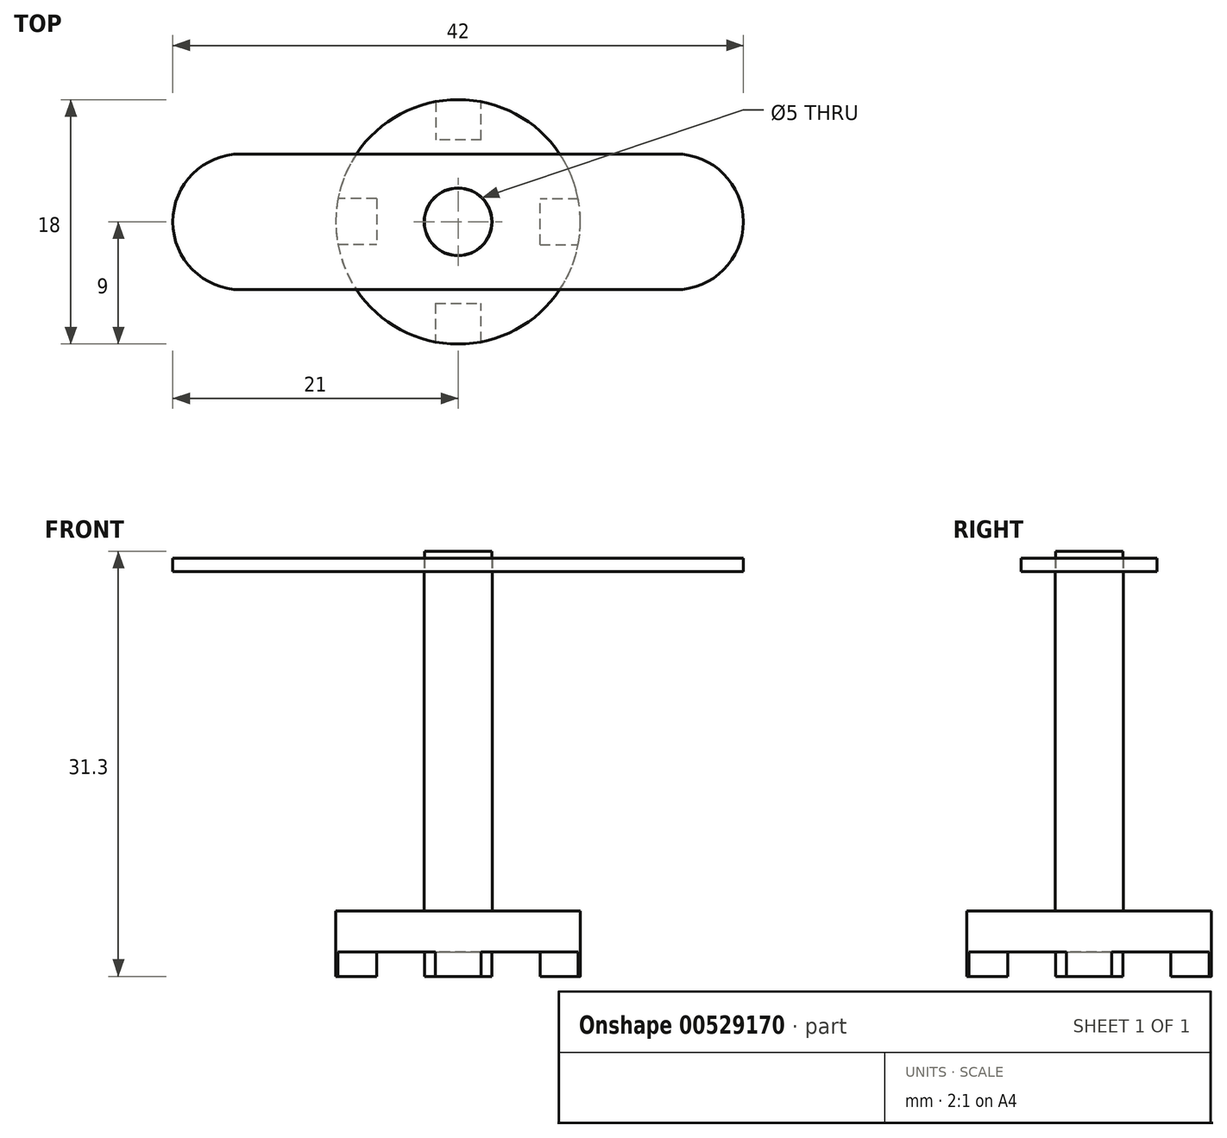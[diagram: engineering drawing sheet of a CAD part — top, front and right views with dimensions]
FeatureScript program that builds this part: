
annotation { "Feature Type Name" : "Feature", "Feature Type Description" : "" }
export const myFeature = defineFeature(function(context is Context, id is Id, definition is map)
    precondition{}
    {
        {
            var Q0;
            Q0=qCreatedBy(makeId("Top.planeOp"),FACE);
            var sketch = newSketch(context, id + "F0", { "sketchPlane" : qUnion([Q0])});
            skCircle(sketch, "E0", {"center": v(0, 0) * mm, "radius": 5 * mm});
            skCircle(sketch, "E1", {"center": v(0, 0) * mm, "radius": 9 * mm});
            skCircle(sketch, "E2", {"center": v(0, 0) * mm, "radius": 2.5 * mm});
            skSolve(sketch);
        }
        {
            var Q0;
            Q0=makeQuery(id+"F0.imprint","IMPRINT",FACE,{"disambiguationData":[TD([[makeQuery(id+"F0.imprint","IMPRINT",EDGE,{"derivedFrom":sQuery(id+"F0.wireOp",EDGE,"E2")}),1.0]])]});
            extrude(context, id + "F1", {"entities" : qUnion([Q0]), "depth" : 25 * mm, "offsetDistance" : 25 * mm});
        }
        {
            var Q0;
            Q0=makeQuery(id+"F0.imprint","IMPRINT",FACE,{"disambiguationData":[TD([[makeQuery(id+"F0.imprint","IMPRINT",EDGE,{"derivedFrom":sQuery(id+"F0.wireOp",EDGE,"E0")}),-1.0]])]});
            var Q1;
            Q1=makeQuery(id+"F0.imprint","IMPRINT",FACE,{"disambiguationData":[TD([[makeQuery(id+"F0.imprint","IMPRINT",EDGE,{"derivedFrom":sQuery(id+"F0.wireOp",EDGE,"E0")}),1.0]])]});
            var Q2;
            Q2=makeQuery(id+"F0.imprint","IMPRINT",FACE,{"disambiguationData":[TD([[makeQuery(id+"F0.imprint","IMPRINT",EDGE,{"derivedFrom":sQuery(id+"F0.wireOp",EDGE,"E2")}),1.0]])]});
            extrude(context, id + "F2", {"entities" : qUnion([Q0, Q1, Q2]), "operationType" : NewBodyOperationType.ADD, "oppositeDirection" : true, "depth" : 3 * mm, "offsetDistance" : 25 * mm});
        }
        {
            var Q0;
            Q0=makeQuery(id+"F2.opExtrude","CAP_FACE",FACE,{"disambiguationData":[OSD([sQuery(id+"F0.wireOp",EDGE,"E1")])],"isStart":false});
            var sketch = newSketch(context, id + "F3", { "sketchPlane" : qUnion([Q0])});
            skCircle(sketch, "E3", {"center": v(0, 0) * mm, "radius": 2.48 * mm});
            skLineSegment(sketch, "E4", {"start": v(0, 0) * mm, "end": v(0, 6) * mm, "construction": true});
            skLineSegment(sketch, "E5", {"start": v(-1.68, 6) * mm, "end": v(-1.68, 13) * mm});
            skLineSegment(sketch, "E6", {"start": v(-1.68, 13) * mm, "end": v(1.67, 13) * mm});
            skLineSegment(sketch, "E7", {"start": v(1.67, 13) * mm, "end": v(1.67, 6) * mm});
            skLineSegment(sketch, "E8", {"start": v(-1.68, 6) * mm, "end": v(1.67, 6) * mm});
            skLineSegment(sketch, "E9.1.0", {"start": v(-6, -1.7) * mm, "end": v(-13, -1.7) * mm});
            skLineSegment(sketch, "E9.1.1", {"start": v(-13, 1.65) * mm, "end": v(-6, 1.65) * mm});
            skLineSegment(sketch, "E9.1.2", {"start": v(-13, -1.7) * mm, "end": v(-13, 1.65) * mm});
            skLineSegment(sketch, "E9.1.3", {"start": v(-6, -1.7) * mm, "end": v(-6, 1.65) * mm});
            skLineSegment(sketch, "E9.2.0", {"start": v(1.7, -6.02) * mm, "end": v(1.7, -13.02) * mm});
            skLineSegment(sketch, "E9.2.1", {"start": v(-1.65, -13.02) * mm, "end": v(-1.65, -6.03) * mm});
            skLineSegment(sketch, "E9.2.2", {"start": v(1.7, -13.02) * mm, "end": v(-1.65, -13.02) * mm});
            skLineSegment(sketch, "E9.2.3", {"start": v(1.7, -6.02) * mm, "end": v(-1.65, -6.03) * mm});
            skPoint(sketch, "E9.center", {"position": v(0.01, -0.01) * mm});
            skLineSegment(sketch, "E10.1.3.0", {"start": v(6.02, 1.67) * mm, "end": v(13.02, 1.67) * mm});
            skLineSegment(sketch, "E10.3.3.0", {"start": v(13.02, -1.67) * mm, "end": v(6.03, -1.67) * mm});
            skLineSegment(sketch, "E10.6.3.0", {"start": v(13.02, 1.67) * mm, "end": v(13.02, -1.67) * mm});
            skLineSegment(sketch, "E10.9.3.0", {"start": v(6.02, 1.67) * mm, "end": v(6.03, -1.67) * mm});
            skSolve(sketch);
        }
        {
            var Q0;
            Q0=makeQuery(id+"F3.imprint","IMPRINT",FACE,{"disambiguationData":[TD([[makeQuery(id+"F3.imprint","IMPRINT",EDGE,{"derivedFrom":sQuery(id+"F3.wireOp",EDGE,"E3")}),1.0]])]});
            var Q1;
            {var subQ0=sQuery(id+"F3.wireOp",EDGE,"E9.1.3");Q1=makeQuery(id+"F3.imprint","IMPRINT",FACE,{"disambiguationData":[TD([[makeQuery(id+"F3.imprint","IMPRINT",EDGE,{"derivedFrom":subQ0}),1.0]])]});}
            var Q2;
            {var subQ0=sQuery(id+"F3.wireOp",EDGE,"E8");Q2=makeQuery(id+"F3.imprint","IMPRINT",FACE,{"disambiguationData":[TD([[makeQuery(id+"F3.imprint","IMPRINT",EDGE,{"derivedFrom":subQ0}),1.0]])]});}
            var Q3;
            {var subQ0=sQuery(id+"F3.wireOp",EDGE,"E10.9.3.0");Q3=makeQuery(id+"F3.imprint","IMPRINT",FACE,{"disambiguationData":[TD([[makeQuery(id+"F3.imprint","IMPRINT",EDGE,{"derivedFrom":subQ0}),1.0]])]});}
            var Q4;
            {var subQ0=sQuery(id+"F3.wireOp",EDGE,"E9.2.3");Q4=makeQuery(id+"F3.imprint","IMPRINT",FACE,{"disambiguationData":[TD([[makeQuery(id+"F3.imprint","IMPRINT",EDGE,{"derivedFrom":subQ0}),1.0]])]});}
            extrude(context, id + "F4", {"entities" : qUnion([Q0, Q1, Q2, Q3, Q4]), "operationType" : NewBodyOperationType.ADD, "depth" : 1.8 * mm, "offsetDistance" : 25 * mm});
        }
        {
            var Q0;
            Q0=makeQuery(id+"F1.opExtrude","CAP_FACE",FACE,{"disambiguationData":[OSD([sQuery(id+"F0.wireOp",EDGE,"E2")])],"isStart":false});
            var sketch = newSketch(context, id + "F5", { "sketchPlane" : qUnion([Q0])});
            skCircle(sketch, "E11", {"center": v(0, 0) * mm, "radius": 2.48 * mm});
            skLineSegment(sketch, "E12", {"start": v(0, 0) * mm, "end": v(-16, 0) * mm, "construction": true});
            skLineSegment(sketch, "E13", {"start": v(0, 0) * mm, "end": v(16, 0) * mm, "construction": true});
            skArc(sketch, "E14", {"start": v(-16, 5) * mm, "mid": v(-21, 0) * mm, "end": v(-16, -5) * mm});
            skArc(sketch, "E15", {"start": v(16, -5) * mm, "mid": v(21, 0) * mm, "end": v(16, 5) * mm});
            skLineSegment(sketch, "E16", {"start": v(-16, 5) * mm, "end": v(16, 5) * mm});
            skLineSegment(sketch, "E17", {"start": v(16, -5) * mm, "end": v(-16, -5) * mm});
            skCircle(sketch, "E18", {"center": v(0, 0) * mm, "radius": 4 * mm});
            skSolve(sketch);
        }
        {
            var Q0;
            Q0=makeQuery(id+"F5.imprint","IMPRINT",FACE,{"disambiguationData":[TD([[makeQuery(id+"F5.imprint","IMPRINT",EDGE,{"derivedFrom":sQuery(id+"F5.wireOp",EDGE,"E11")}),1.0]])]});
            extrude(context, id + "F6", {"entities" : qUnion([Q0]), "operationType" : NewBodyOperationType.ADD, "depth" : 1.5 * mm, "offsetDistance" : 25 * mm});
        }
        {
            var Q0;
            Q0=makeQuery(id+"F5.imprint","IMPRINT",FACE,{"disambiguationData":[TD([[makeQuery(id+"F5.imprint","IMPRINT",EDGE,{"derivedFrom":sQuery(id+"F5.wireOp",EDGE,"E14")}),1.0]])]});
            var Q1;
            Q1=makeQuery(id+"F5.imprint","IMPRINT",FACE,{"disambiguationData":[TD([[makeQuery(id+"F5.imprint","IMPRINT",EDGE,{"derivedFrom":sQuery(id+"F5.wireOp",EDGE,"E18")}),1.0]])]});
            extrude(context, id + "F7", {"entities" : qUnion([Q0, Q1]), "depth" : 1 * mm, "offsetDistance" : 25 * mm});
        }
    });
